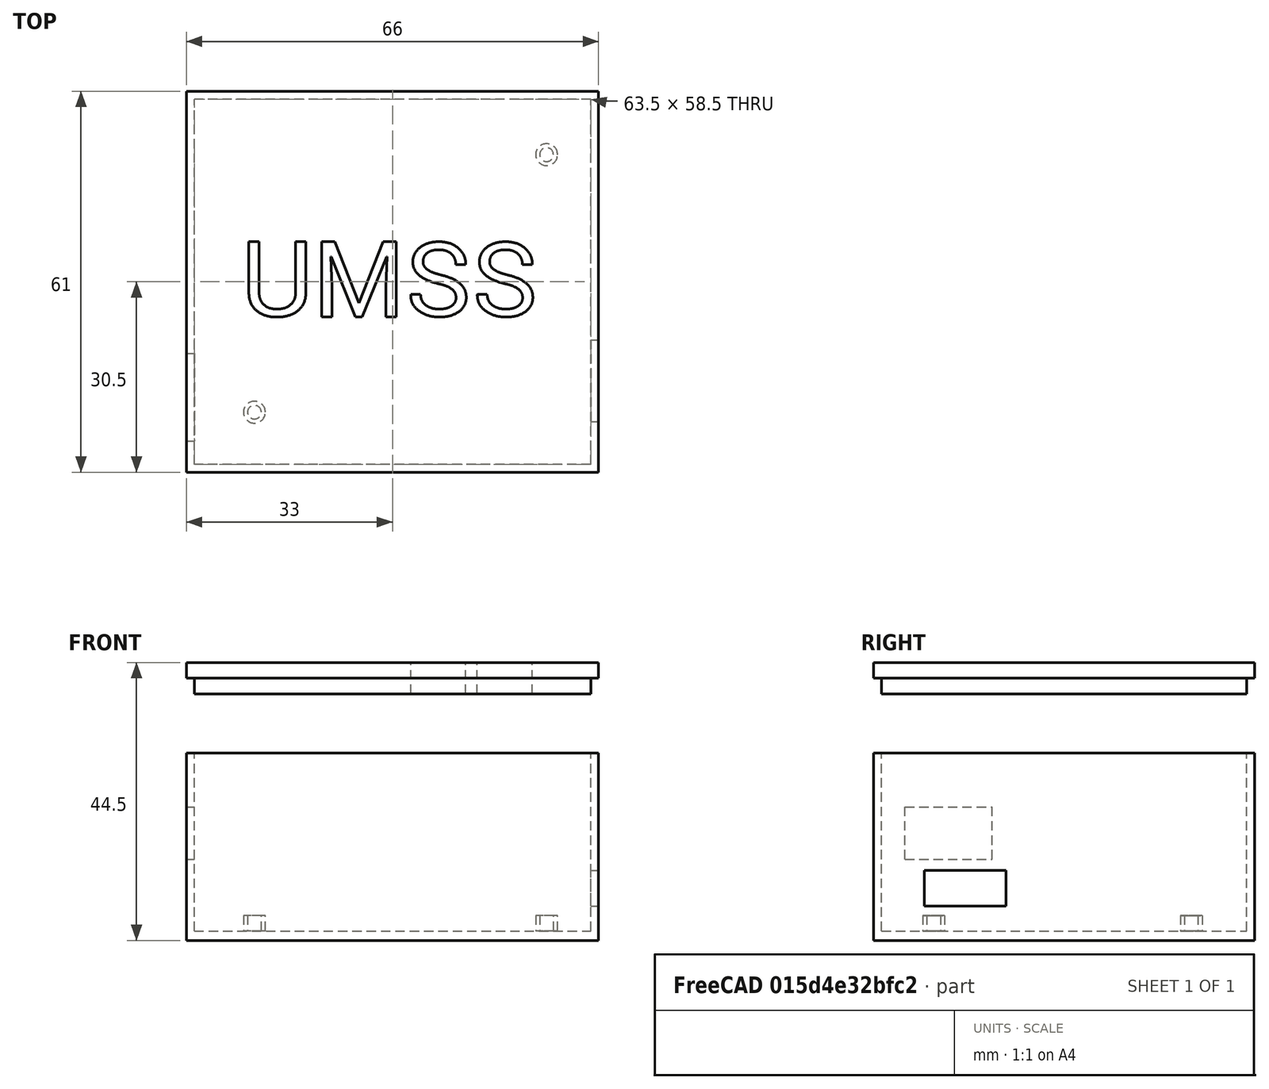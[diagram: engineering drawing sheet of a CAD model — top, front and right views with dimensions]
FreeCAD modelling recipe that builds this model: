
FCSTD DOCUMENT  (FreeCAD 0.17R13541 (Git))
Label: case_back
License: All rights reserved
LicenseURL: http://en.wikipedia.org/wiki/All_rights_reserved
objects: Part::Box×8, Part::Cut×4, Part::MultiFuse×3, Part::Extrusion×2, Sketcher::SketchObject×1, Part::Part2DObjectPython×1
note: 19 computed .brp shape members not serialized (recipe doc carries the construction recipe); baked Part::Feature solids carry a one-line shape summary decoded from their .brp

FEATURE [Part::Box] Box  label="Cubo"
  AttacherType = Attacher::AttachEngine3D
  Height = 1.5
  Length = 55.5
  Width = 51.3
FEATURE [Part::Box] Box001  label="Cubo001"
  AttacherType = Attacher::AttachEngine3D
  Height = 1.5
  Length = 66
  Placement = pos=(-5,-5,0) rot=(0,0,1;0rad)
  Width = 61
FEATURE [Part::Box] Box002  label="Cubo002"
  AttacherType = Attacher::AttachEngine3D
  Height = 30
  Length = 63.5
  Placement = pos=(-3.75,-3.75,1.5) rot=(0,0,1;0rad)
  Width = 58.5
FEATURE [Part::Box] Box003  label="Cubo003"
  AttacherType = Attacher::AttachEngine3D
  Height = 5.7
  Length = 7
  Placement = pos=(51,3.1,1.5) rot=(0,0,1;0rad)
  Width = 13.1
FEATURE [Part::MultiFuse] Fusion
  Placement = pos=(3,0,4) rot=(0,0,1;0rad)
  Shapes = -> [Box003,Box]
FEATURE [Part::Box] Box004  label="Cubo004"
  AttacherType = Attacher::AttachEngine3D
  Height = 30
  Length = 66
  Placement = pos=(-5,-5,0) rot=(0,0,1;0rad)
  Width = 61
FEATURE [Sketcher::SketchObject] Sketch
  MapMode = 2
  Placement = pos=(-5,-5,0) rot=(0,0,1;0rad)
  Support = -> [Box001]
  sketch-geometry (4):
    g0: Circle CenterX=57.6748 CenterY=50.8585 CenterZ=0 NormalX=0 NormalY=0 NormalZ=1 AngleXU=0 Radius=1.75
    g1: Circle CenterX=10.8758 CenterY=9.60571 CenterZ=0 NormalX=0 NormalY=0 NormalZ=1 AngleXU=0 Radius=1.75
    g2: Circle CenterX=10.8758 CenterY=9.60571 CenterZ=0 NormalX=0 NormalY=0 NormalZ=1 AngleXU=0 Radius=1.1
    g3: Circle CenterX=57.6748 CenterY=50.8585 CenterZ=0 NormalX=0 NormalY=0 NormalZ=1 AngleXU=0 Radius=1.1
  constraints (6):
    c: Radius(g1) = 1.75
    c: Coincident(g2,g1)
    c: Radius(g2) = 1.1
    c: Radius(g0) = 1.75
    c: Coincident(g3,g0)
    c: Radius(g3) = 1.1
FEATURE [Part::Extrusion] Extrude
  Base = -> Sketch
  Dir = (0,0,1)
  DirMode = 2
  FaceMakerClass = Part::FaceMakerBullseye
  LengthFwd = 4
  LengthRev = 0
  Solid = true
  Symmetric = false
FEATURE [Part::Box] Box005  label="Cubo005"
  AttacherType = Attacher::AttachEngine3D
  Height = 8.4
  Length = 10
  Placement = pos=(-5,0,13) rot=(0,0,1;0rad)
  Width = 14
FEATURE [Part::Box] Box006  label="copia"
  AttacherType = Attacher::AttachEngine3D
  Height = 4
  Length = 63.5
  Placement = pos=(-3.75,-3.75,28.5) rot=(0,0,1;0rad)
  Width = 58.5
FEATURE [Part::Cut] Cut
  Base = -> Box004
  Tool = -> Box002
FEATURE [Part::Box] Box007  label="Cubo006"
  AttacherType = Attacher::AttachEngine3D
  Height = 2.5
  Length = 66
  Placement = pos=(-5,-5,31) rot=(0,0,1;0rad)
  Width = 61
FEATURE [Part::MultiFuse] Fusion001
  Placement = pos=(0,0,11) rot=(0,0,1;0rad)
  Shapes = -> [Box007,Box006]
FEATURE [Part::Cut] Cut001
  Base = -> Cut
  Tool = -> Box005
FEATURE [Part::Cut] Cut002
  Base = -> Cut001
  Tool = -> Fusion
FEATURE [Part::MultiFuse] Fusion002
  Shapes = -> [Cut002,Box001,Extrude]
FEATURE [Part::Part2DObjectPython] ShapeString  # Draft 2D object (typed FeaturePython)
  FontFile = <path>
  Placement = pos=(3.76,19.83,44.5) rot=(0,0,1;0rad)
  Size = 15
  String = UMSS
  Tracking = 0
FEATURE [Part::Extrusion] Extrude001
  Base = -> ShapeString
  Dir = (0,0,1)
  DirMode = 2
  FaceMakerClass = Part::FaceMakerBullseye
  LengthFwd = 7
  LengthRev = 0
  Placement = pos=(0,0,-6.5) rot=(0,0,1;0rad)
  Solid = false
  Symmetric = false
FEATURE [Part::Cut] Cut003
  Base = -> Fusion001
  Tool = -> Extrude001
note: 1 file-system path scrubbed to <path> (originals preserved in the JSON sidecar)
